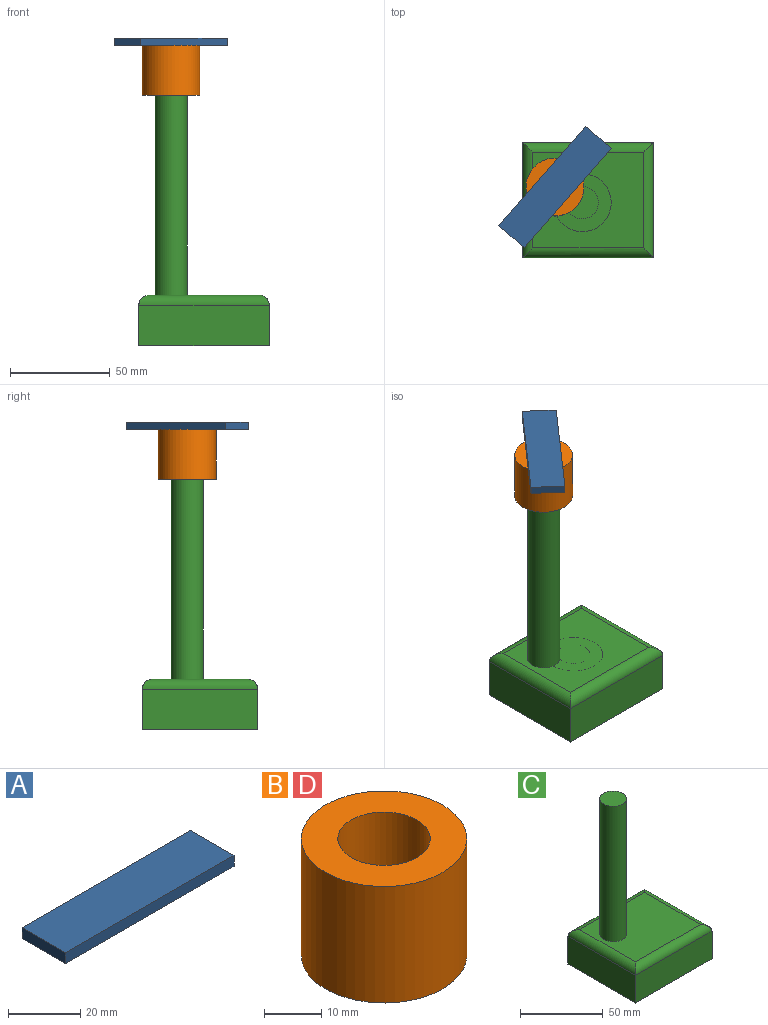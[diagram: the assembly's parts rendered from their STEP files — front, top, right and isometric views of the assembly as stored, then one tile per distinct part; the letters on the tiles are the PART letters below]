
ASSEMBLY  parts=4 mates=2
PART A: 6 faces, bbox 66.1x17x3.7 mm
  f0: plane 66.07x3.69mm, normal (0,1,0), area 243.8mm2, adj f1,f3,f4,f5
  f1: plane 17.03x3.69mm, normal (-1,0,0), area 62.8mm2, adj f0,f2,f4,f5
  f2: plane 66.07x3.69mm, normal (0,-1,0), area 243.8mm2, adj f1,f3,f4,f5
  f3: plane 17.03x3.69mm, normal (1,0,0), area 62.8mm2, adj f0,f2,f4,f5
  f4: plane 66.07x17.03mm, normal (0,0,1), area 1125mm2, adj f0,f1,f2,f3
  f5: plane 66.07x17.03mm, normal (0,0,-1), area 1125mm2, adj f0,f1,f2,f3
PART B: 4 faces, bbox 29x29x25 mm
  f0: cylinder r=8.1mm len=25mm, axis (0,0,-1), area 1272.3mm2, adj f2,f3
  f1: cylinder r=14.5mm len=29mm, axis (0,0,-1), area 2277.5mm2, adj f2,f3
  f2: plane 29x29mm, normal (0,0,1), area 454.3mm2, adj f0,f1
  f3: plane 29x29mm, normal (0,0,-1), area 454.3mm2, adj f0,f1
PART C: 12 faces, bbox 65.3x57.7x125.4 mm
  f0: plane 65.3x20.4mm, normal (0,1,0), area 1332.2mm2, adj f1,f3,f5,f6
  f1: plane 57.66x20.4mm, normal (-1,0,0), area 1176.2mm2, adj f0,f2,f5,f7
  f2: plane 65.3x20.4mm, normal (0,-1,0), area 1332.2mm2, adj f1,f3,f5,f9
  f3: plane 57.66x20.4mm, normal (1,0,0), area 1176.2mm2, adj f0,f2,f5,f8
  f4: plane 55.3x47.66mm, normal (0,0,1), area 2431.8mm2, adj f6,f7,f8,f9,f10
  f5: plane 65.3x57.66mm, normal (0,0,-1), area 3765.3mm2, adj f0,f1,f2,f3
  f6: cylinder r=5mm len=65.3mm, axis (1,0,0), area 484.3mm2, adj f0,f4,f7,f8
  f7: cylinder r=5mm len=57.66mm, axis (0,1,0), area 424.3mm2, adj f1,f4,f6,f9
  f8: cylinder r=5mm len=57.66mm, axis (0,-1,0), area 424.3mm2, adj f3,f4,f6,f9
  f9: cylinder r=5mm len=65.3mm, axis (-1,0,0), area 484.3mm2, adj f2,f4,f7,f8
  f10: cylinder r=8.06mm len=100mm, axis (0,0,-1), area 5061.5mm2, adj f4,f11
  f11: plane 16.11x16.11mm, normal (0,0,1), area 203.9mm2, adj f10
PART D: same geometry as B
PLACE A rot(axis=(0,0,1),48.8deg) t=(-46.24,-60.36,150.4)mm
PLACE B rot(axis=(0,0,-1),131.2deg) t=(-13.63,7.63,125.4)mm
PLACE C at identity fixed
PLACE D at identity
MATE fastened B.f0 <-> A.f5  axis (0,0,1) through (-13.63,7.63,150.4)mm
MATE revolute B.f0 <-> C.f10  axis (0,0,-1) through (-13.63,7.63,125.4)mm
